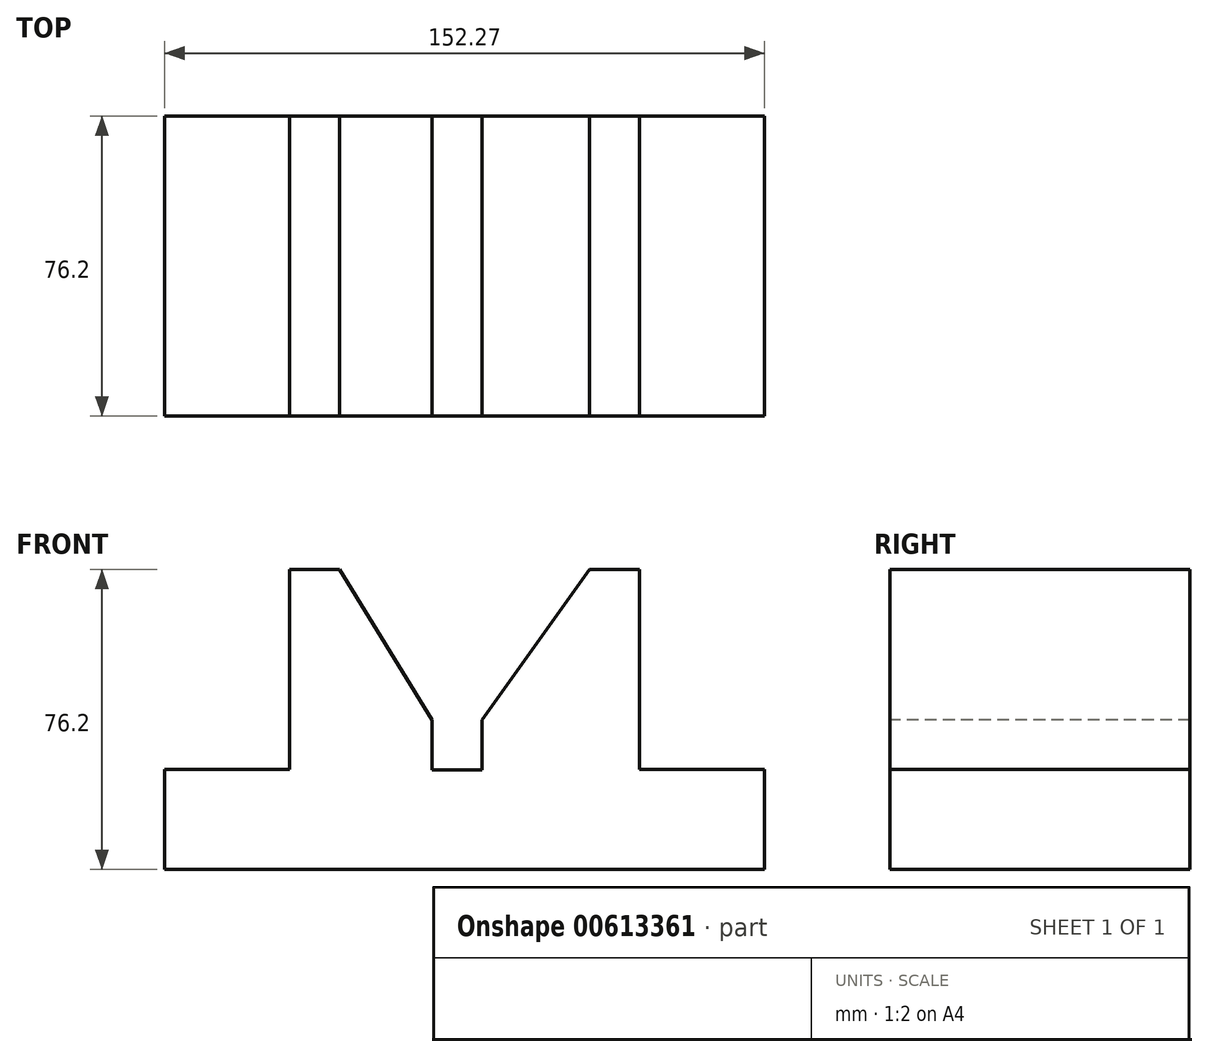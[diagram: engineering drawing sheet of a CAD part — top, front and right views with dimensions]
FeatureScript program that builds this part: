
annotation { "Feature Type Name" : "Feature", "Feature Type Description" : "" }
export const myFeature = defineFeature(function(context is Context, id is Id, definition is map)
    precondition{}
    {
        {
            var Q0;
            Q0=qCreatedBy(makeId("Front.planeOp"),FACE);
            var sketch = newSketch(context, id + "F0", { "sketchPlane" : qUnion([Q0])});
            skLineSegment(sketch, "E0", {"start": v(0, 0) * mm, "end": v(152.27, 0) * mm});
            skLineSegment(sketch, "E1", {"start": v(152.27, 0) * mm, "end": v(152.27, 25.4) * mm});
            skLineSegment(sketch, "E2", {"start": v(120.52, 76.2) * mm, "end": v(107.82, 76.2) * mm});
            skLineSegment(sketch, "E3", {"start": v(0, 25.4) * mm, "end": v(0, 0) * mm});
            skLineSegment(sketch, "E4", {"start": v(31.75, 76.2) * mm, "end": v(31.75, 25.4) * mm});
            skLineSegment(sketch, "E5", {"start": v(31.75, 25.4) * mm, "end": v(0, 25.4) * mm});
            skLineSegment(sketch, "E6", {"start": v(120.52, 76.2) * mm, "end": v(120.52, 25.4) * mm});
            skLineSegment(sketch, "E7", {"start": v(120.52, 25.4) * mm, "end": v(152.27, 25.4) * mm});
            skLineSegment(sketch, "E8", {"start": v(67.89, 37.95) * mm, "end": v(67.89, 25.25) * mm});
            skLineSegment(sketch, "E9", {"start": v(67.89, 25.25) * mm, "end": v(80.59, 25.25) * mm});
            skLineSegment(sketch, "E10", {"start": v(80.59, 25.25) * mm, "end": v(80.59, 37.95) * mm});
            skLineSegment(sketch, "E11.trimOffspring", {"start": v(44.45, 76.2) * mm, "end": v(31.75, 76.2) * mm});
            skLineSegment(sketch, "E12", {"start": v(31.75, 76.2) * mm, "end": v(44.45, 76.2) * mm});
            skLineSegment(sketch, "E13", {"start": v(44.45, 76.2) * mm, "end": v(67.89, 37.95) * mm});
            skLineSegment(sketch, "E14", {"start": v(107.82, 76.2) * mm, "end": v(80.59, 37.95) * mm});
            skSolve(sketch);
        }
        {
            var Q0;
            Q0 = qSketchRegion(id + "F0", true);
            extrude(context, id + "F1", {"entities" : qUnion([Q0]), "oppositeDirection" : true, "depth" : 76.2 * mm, "offsetDistance" : 25.4 * mm});
        }
    });
